# Revit family: Smart Sensor NeuronGrid MS660230
name_source: partatom
category: Datengeräte
units: mm (PartAtom-declared; Revit-internal decimal feet)

## family parameters
Arbeitsebenenbasiert = Nein
Beim Laden mit Abzugskörper schneiden = Nein
Bemaßung runder Anschluss = Durchmesser verwenden
Beschriftungsausrichtung beibehalten = Nein
Gemeinsam genutzt = Nein
Immer vertikal = Ja
OmniClass-Nummer = 23.85.50.17
OmniClass-Titel = Communication and Data Processing Equipment
Raumberechnungspunkt = Nein
Teiletyp = Normal

## types (1)
- Smart Sensor NeuronGrid MS660230
    Anschluss 1 = 2 x Sensor ports RJ 45
    Artikelnummer = MS660230
    Beschreibung = Smart Sensor NeuronGrid (Radar)
    Eigenschaft 1 = Lichtintensität
    Eigenschaft 2 = Bewegung
    Eigenschaft 3 = Temperatur
    Eigenschaft 4 = Luftfeuchte
    Eigenschaft 5 = Integrierter Beacon
    Eigenschaft 6 = Luftqualität
    Erweiterung = via Buskopplung
    Hersteller = MICROSENS
    Vorgabe-Ansicht = 0 mm  [stored 0 ft]

note: [stored X ft] marks values corroborated as IEEE doubles in the binary element streams (Revit-internal decimal feet)
